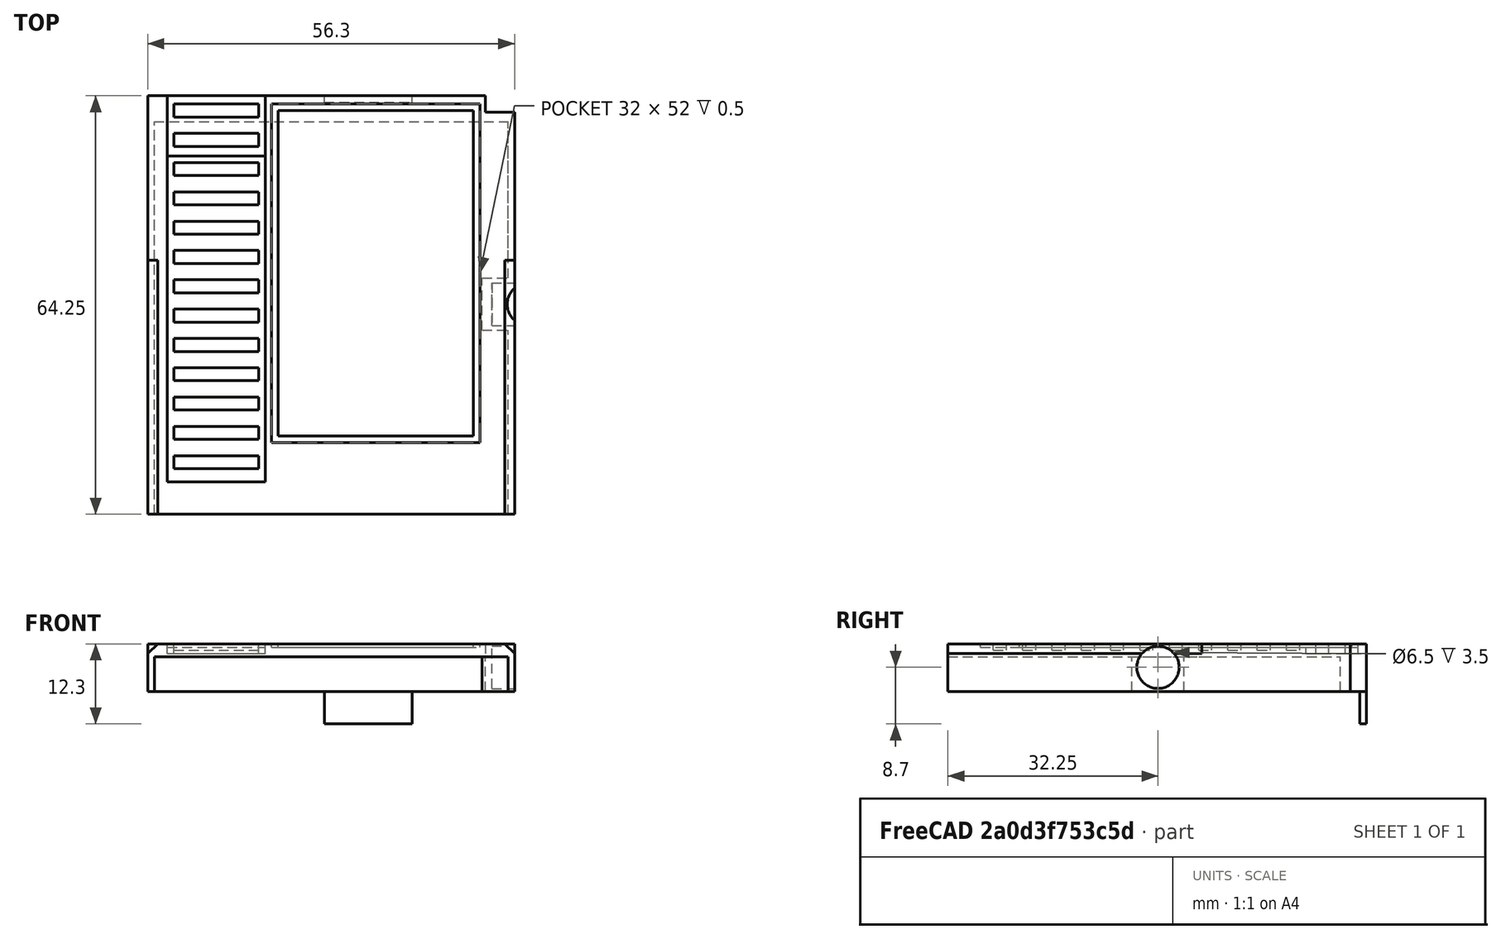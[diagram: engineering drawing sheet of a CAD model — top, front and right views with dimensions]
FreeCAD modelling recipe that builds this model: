
FCSTD DOCUMENT  (FreeCAD 0.18R16131 (Git))
Label: GBC_cart_cover
License: All rights reserved
LicenseURL: http://en.wikipedia.org/wiki/All_rights_reserved
objects: Part::Box×26, Part::Cut×7, Part::MultiFuse×3, Part::Chamfer×1, Part::Cylinder×1
note: 38 computed .brp shape members not serialized (recipe doc carries the construction recipe); baked Part::Feature solids carry a one-line shape summary decoded from their .brp

FEATURE [Part::Box] Box  label="Cube(outer_base)"
  AttacherType = Attacher::AttachEngine3D
  Height = 5.3
  Length = 56.3
  Width = 64.25
FEATURE [Part::Box] Box001  label="Cube(corner_inner)"
  AttacherType = Attacher::AttachEngine3D
  Height = 5.3
  Length = 4.5
  Placement = pos=(51.8,61.75,0) rot=(0,0,1;0rad)
  Width = 2.5
FEATURE [Part::Box] Box007  label="Cube(top_cover_top_half)"
  AttacherType = Attacher::AttachEngine3D
  Height = 2
  Length = 56.3
  Placement = pos=(0,39,5.3) rot=(0,0,1;0rad)
  Width = 25.25
FEATURE [Part::Box] Box008  label="Cube001(top_cover_bottom_half)"
  AttacherType = Attacher::AttachEngine3D
  Height = 2
  Length = 56.3
  Placement = pos=(0,0,5.3) rot=(0,0,1;0rad)
  Width = 39
FEATURE [Part::Box] Box010  label="Cube(top_corner_cut)"
  AttacherType = Attacher::AttachEngine3D
  Height = 10
  Length = 10
  Placement = pos=(51.8,61.75,0) rot=(0,0,1;0rad)
  Width = 10
FEATURE [Part::Cut] Cut006
  Base = -> Box007
  Tool = -> Box010
FEATURE [Part::Box] Box017  label="Cube(game_lable_inner)"
  AttacherType = Attacher::AttachEngine3D
  Height = 0.5
  Length = 30
  Placement = pos=(20,12,6.8) rot=(0,0,1;0rad)
  Width = 50
FEATURE [Part::Box] Box018  label="Cube(cube_strips)"
  AttacherType = Attacher::AttachEngine3D
  Height = 0.5
  Length = 15
  Placement = pos=(3,5,6.8) rot=(0,0,1;0rad)
  Width = 53
FEATURE [Part::Box] Box019  label="Cube(cube_strip_top)"
  AttacherType = Attacher::AttachEngine3D
  Height = 1.5
  Length = 15
  Placement = pos=(3,55,5.8) rot=(0,0,1;0rad)
  Width = 9.25
FEATURE [Part::Box] Box020  label="Cube(ladders)"
  AttacherType = Attacher::AttachEngine3D
  Height = 1
  Length = 13
  Placement = pos=(4,7,6.3) rot=(0,0,1;0rad)
  Width = 2
FEATURE [Part::Box] Box021  label="Cube(ladders)001"
  AttacherType = Attacher::AttachEngine3D
  Height = 1
  Length = 13
  Placement = pos=(4,11.5,6.3) rot=(0,0,1;0rad)
  Width = 2
FEATURE [Part::Box] Box022  label="Cube(ladders)002"
  AttacherType = Attacher::AttachEngine3D
  Height = 1
  Length = 13
  Placement = pos=(4,16,6.3) rot=(0,0,1;0rad)
  Width = 2
FEATURE [Part::Box] Box023  label="Cube(ladders)003"
  AttacherType = Attacher::AttachEngine3D
  Height = 1
  Length = 13
  Placement = pos=(4,20.5,6.3) rot=(0,0,1;0rad)
  Width = 2
FEATURE [Part::Box] Box024  label="Cube(ladders)004"
  AttacherType = Attacher::AttachEngine3D
  Height = 1
  Length = 13
  Placement = pos=(4,25,6.3) rot=(0,0,1;0rad)
  Width = 2
FEATURE [Part::Box] Box025  label="Cube(ladders)005"
  AttacherType = Attacher::AttachEngine3D
  Height = 1
  Length = 13
  Placement = pos=(4,29.5,6.3) rot=(0,0,1;0rad)
  Width = 2
FEATURE [Part::Box] Box029  label="Cube(cube_strip_top_outer)"
  AttacherType = Attacher::AttachEngine3D
  Height = 1.5
  Length = 17
  Placement = pos=(2,55,5.8) rot=(0,0,1;0rad)
  Width = 9.25
FEATURE [Part::MultiFuse] Fusion003
  Shapes = -> [Cut006,Box029]
FEATURE [Part::Cut] Cut008
  Base = -> Fusion003
  Tool = -> Box019
FEATURE [Part::Box] Box030  label="Cube(ladders)009"
  AttacherType = Attacher::AttachEngine3D
  Height = 1
  Length = 13
  Placement = pos=(4,34,6.3) rot=(0,0,1;0rad)
  Width = 2
FEATURE [Part::Box] Box031  label="Cube(ladders)010"
  AttacherType = Attacher::AttachEngine3D
  Height = 1
  Length = 13
  Placement = pos=(4,38.5,6.3) rot=(0,0,1;0rad)
  Width = 2
FEATURE [Part::Box] Box032  label="Cube(ladders)011"
  AttacherType = Attacher::AttachEngine3D
  Height = 1
  Length = 13
  Placement = pos=(4,43,6.3) rot=(0,0,1;0rad)
  Width = 2
FEATURE [Part::Box] Box034  label="Cube(ladders)013"
  AttacherType = Attacher::AttachEngine3D
  Height = 1
  Length = 13
  Placement = pos=(4,47.5,6.3) rot=(0,0,1;0rad)
  Width = 2
FEATURE [Part::Box] Box035  label="Cube(ladders)014"
  AttacherType = Attacher::AttachEngine3D
  Height = 1
  Length = 13
  Placement = pos=(4,52,6.3) rot=(0,0,1;0rad)
  Width = 2
FEATURE [Part::Box] Box038  label="Cube(ladders)017"
  AttacherType = Attacher::AttachEngine3D
  Height = 1.5
  Length = 13
  Placement = pos=(4,56.5,5.8) rot=(0,0,1;0rad)
  Width = 2
FEATURE [Part::Box] Box040  label="Cube(ladders)019"
  AttacherType = Attacher::AttachEngine3D
  Height = 1.5
  Length = 13
  Placement = pos=(4,61,5.8) rot=(0,0,1;0rad)
  Width = 2
FEATURE [Part::Box] Box041  label="Cube(game_lable_outer)"
  AttacherType = Attacher::AttachEngine3D
  Height = 0.5
  Length = 32
  Placement = pos=(19,11,6.8) rot=(0,0,1;0rad)
  Width = 52
FEATURE [Part::Chamfer] Chamfer
  Base = -> Box008
  Edges = 2 edges r=1.5: [Edge2,Edge6]
FEATURE [Part::MultiFuse] Fusion004
  Shapes = -> [Cut008,Chamfer]
FEATURE [Part::Cut] Cut012
  Base = -> Fusion004
  Tool = -> Box018
FEATURE [Part::Cut] Cut013
  Base = -> Cut012
  Tool = -> Box041
FEATURE [Part::Box] Box042  label="Cube(outer_base)001"
  AttacherType = Attacher::AttachEngine3D
  Height = 5.3
  Length = 54.3
  Placement = pos=(1,0,0) rot=(0,0,1;0rad)
  Width = 60.25
FEATURE [Part::Cut] Cut
  Base = -> Box
  Tool = -> Box001
FEATURE [Part::Cut] Cut014
  Base = -> Cut
  Tool = -> Box042
FEATURE [Part::Box] Box043  label="Cube(sd_card_cover)"
  AttacherType = Attacher::AttachEngine3D
  Height = 5
  Length = 13.5
  Placement = pos=(27.1,63.25,-5) rot=(0,0,1;0rad)
  Width = 1
FEATURE [Part::Cylinder] Cylinder  label="Cylinder(magnet)"
  Angle = 360
  AttacherType = Attacher::AttachEngine3D
  Height = 3.5
  Placement = pos=(52.8,32.25,3.7) rot=(0,1,0;1.5708rad)
  Radius = 3.25
FEATURE [Part::Box] Box044  label="Cube(magnet_block)"
  AttacherType = Attacher::AttachEngine3D
  Height = 5.3
  Length = 4
  Placement = pos=(51.3,28.25,0) rot=(0,0,1;0rad)
  Width = 8
FEATURE [Part::MultiFuse] Fusion
  Shapes = -> [Box044,Cut014,Cut013]
FEATURE [Part::Cut] Cut015
  Base = -> Fusion
  Tool = -> Cylinder
